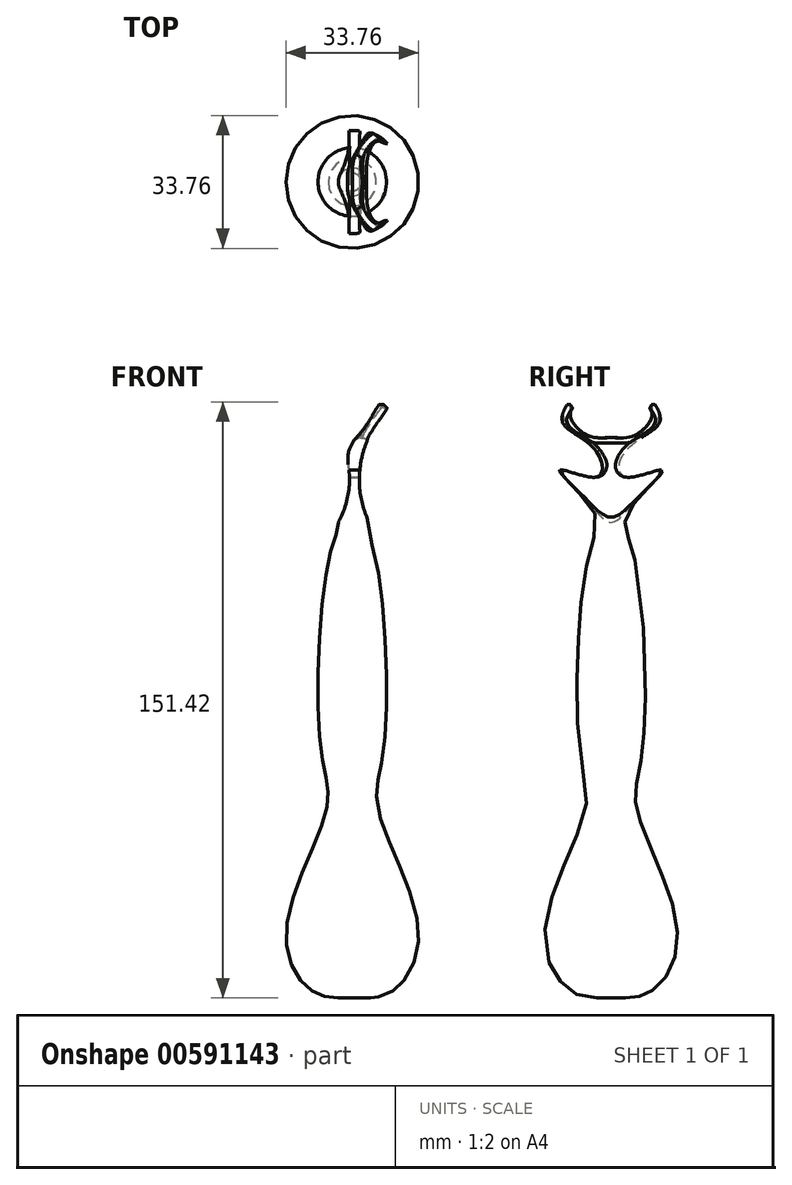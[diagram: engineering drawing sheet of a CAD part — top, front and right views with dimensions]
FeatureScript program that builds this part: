
annotation { "Feature Type Name" : "Feature", "Feature Type Description" : "" }
export const myFeature = defineFeature(function(context is Context, id is Id, definition is map)
    precondition{}
    {
        {
            var Q0;
            Q0=qCreatedBy(makeId("Front.planeOp"),FACE);
            var sketch = newSketch(context, id + "F0", { "sketchPlane" : qUnion([Q0])});
            skLineSegment(sketch, "E0", {"start": v(0, -65.62) * mm, "end": v(0, 64.38) * mm});
            skFitSpline(sketch, "E1", {"points": [v(0, 64.38) * mm, v(-6.2, 64.38) * mm, v(-11.91, 69.45) * mm, v(-12.75, 72.42) * mm], "startDerivative": vector(-17.4, -3.4) * mm, "endDerivative": vector(-1.12, 11.07) * mm});
            skLineSegment(sketch, "E2", {"start": v(-12.75, 72.42) * mm, "end": v(-13.04, 72.42) * mm});
            skFitSpline(sketch, "E3", {"points": [v(-13.04, 72.42) * mm, v(-12.75, 67.5) * mm, v(-4.14, 60.95) * mm, v(-3.52, 54.06) * mm, v(-13.04, 55.7) * mm, v(-4.48, 45.36) * mm, v(-5.61, 34.57) * mm, v(-7.9, -15.91) * mm, v(-6.5, -30.44) * mm, v(-16.85, -61.67) * mm, v(-9.69, -77) * mm, v(0, -78.19) * mm], "startDerivative": vector(-21.06, -99.85) * mm, "endDerivative": vector(134.3, 10.78) * mm});
            skLineSegment(sketch, "E4", {"start": v(0, -78.19) * mm, "end": v(0, -65.62) * mm});
            skSolve(sketch);
        }
        {
            var Q0;
            Q0=makeQuery(id+"F0.imprint","IMPRINT",FACE,{"disambiguationData":[TD([[makeQuery(id+"F0.imprint","IMPRINT",EDGE,{"derivedFrom":sQuery(id+"F0.wireOp",EDGE,"E0")}),1.0]])]});
            var Q1;
            Q1=sQuery(id+"F0.wireOp",EDGE,"E0");
            revolve(context, id + "F1", {"entities" : qUnion([Q0]), "axis" : qUnion([Q1]), "revolveType" : RevolveType.FULL});
        }
        {
            var Q0;
            Q0=qCreatedBy(makeId("Front.planeOp"),FACE);
            var sketch = newSketch(context, id + "F2", { "sketchPlane" : qUnion([Q0])});
            skCircle(sketch, "E5", {"center": v(-23.06, 53.34) * mm, "radius": 22.34 * mm});
            skCircle(sketch, "E6", {"center": v(26.82, 53.34) * mm, "radius": 25.03 * mm});
            skSolve(sketch);
        }
        {
            var Q0;
            Q0 = qSketchRegion(id + "F2", true);
            var Q1;
            Q1=makeQuery(id+"F2.imprint","IMPRINT",FACE,{"disambiguationData":[TD([[makeQuery(id+"F2.imprint","IMPRINT",EDGE,{"derivedFrom":sQuery(id+"F2.wireOp",EDGE,"E6")}),1.0]])]});
            extrude(context, id + "F3", {"entities" : qUnion([Q0, Q1]), "operationType" : NewBodyOperationType.REMOVE, "endBound" : BoundingType.SYMMETRIC, "oppositeDirection" : true, "depth" : 59.2 * mm, "offsetDistance" : 25 * mm});
        }
        {
            var Q0;
            Q0=qCreatedBy(makeId("Front.planeOp"),FACE);
            var sketch = newSketch(context, id + "F4", { "sketchPlane" : qUnion([Q0])});
            skCircle(sketch, "E7", {"center": v(-19.45, 83.07) * mm, "radius": 28.02 * mm});
            skSolve(sketch);
        }
        {
            var Q0;
            Q0=makeQuery(id+"F4.imprint","IMPRINT",FACE,{"disambiguationData":[TD([[makeQuery(id+"F4.imprint","IMPRINT",EDGE,{"derivedFrom":sQuery(id+"F4.wireOp",EDGE,"E7")}),1.0]])]});
            extrude(context, id + "F5", {"entities" : qUnion([Q0]), "operationType" : NewBodyOperationType.REMOVE, "endBound" : BoundingType.SYMMETRIC, "depth" : 90.8 * mm, "offsetDistance" : 25 * mm});
        }
        {
            var Q0;
            Q0=makeQuery(id+"F5.boolean.opBoolean","INTERSECT",EDGE,{"derivedFrom":[makeQuery(id+"F3.boolean.opBoolean","COPY",FACE,{"derivedFrom":makeQuery(id+"F3.opExtrude","SWEPT_FACE",FACE,{"disambiguationData":[OSD([sQuery(id+"F2.wireOp",EDGE,"E5")])]})}),makeQuery(id+"F5.opExtrude","SWEPT_FACE",FACE,{"disambiguationData":[OSD([sQuery(id+"F4.wireOp",EDGE,"E7")])]})]});
            fillet(context, id + "F6", {"entities" : qUnion([Q0]), "radius" : 8.05 * mm, "tangentPropagation" : true, "allowEdgeOverflow" : false});
        }
        {
            var Q0;
            Q0=qCreatedBy(makeId("Right.planeOp"),FACE);
            var sketch = newSketch(context, id + "F7", { "sketchPlane" : qUnion([Q0])});
            skCircle(sketch, "E8", {"center": v(0, 77.34) * mm, "radius": 11.44 * mm});
            skSolve(sketch);
        }
        {
            var Q0;
            Q0 = qSketchRegion(id + "F7", true);
            var Q1;
            Q1=makeQuery(id+"F7.imprint","IMPRINT",FACE,{"disambiguationData":[TD([[makeQuery(id+"F7.imprint","IMPRINT",EDGE,{"derivedFrom":sQuery(id+"F7.wireOp",EDGE,"E8")}),1.0]])]});
            extrude(context, id + "F8", {"entities" : qUnion([Q0, Q1]), "operationType" : NewBodyOperationType.REMOVE, "depth" : 25 * mm, "offsetDistance" : 25 * mm});
        }
        {
            var Q0;
            Q0=makeQuery(id+"F5.boolean.opBoolean","INTERSECT",EDGE,{"derivedFrom":[makeQuery(id+"F1.opRevolve","SWEPT_FACE",FACE,{"disambiguationData":[OSD([sQuery(id+"F0.wireOp",EDGE,"E1")])]}),makeQuery(id+"F5.opExtrude","SWEPT_FACE",FACE,{"disambiguationData":[OSD([sQuery(id+"F4.wireOp",EDGE,"E7")])]})]});
            var Q1;
            Q1=makeQuery(id+"F5.boolean.opBoolean","INTERSECT",EDGE,{"derivedFrom":[makeQuery(id+"F1.opRevolve","SWEPT_FACE",FACE,{"disambiguationData":[OSD([sQuery(id+"F0.wireOp",EDGE,"E1")])]}),makeQuery(id+"F5.opExtrude","SWEPT_FACE",FACE,{"disambiguationData":[OSD([sQuery(id+"F4.wireOp",EDGE,"E7")])]})]});
            var Q2;
            Q2=makeQuery(id+"F6.opFillet","BLEND_EDGE",EDGE,{"disambiguationData":[OD(1.0)],"blendedFrom":[makeQuery(id+"F5.boolean.opBoolean","INTERSECT",EDGE,{"derivedFrom":[makeQuery(id+"F3.boolean.opBoolean","COPY",FACE,{"derivedFrom":makeQuery(id+"F3.opExtrude","SWEPT_FACE",FACE,{"disambiguationData":[OSD([sQuery(id+"F2.wireOp",EDGE,"E5")])]})}),makeQuery(id+"F5.opExtrude","SWEPT_FACE",FACE,{"disambiguationData":[OSD([sQuery(id+"F4.wireOp",EDGE,"E7")])]})]}),makeQuery(id+"F1.opRevolve","SWEPT_FACE",FACE,{"disambiguationData":[OSD([sQuery(id+"F0.wireOp",EDGE,"E1")])]})],"blendedInto":[makeQuery(id+"F1.opRevolve","SWEPT_FACE",FACE,{"disambiguationData":[OSD([sQuery(id+"F0.wireOp",EDGE,"E1")])]})]});
            var Q3;
            Q3=makeQuery(id+"F5.boolean.opBoolean","INTERSECT",EDGE,{"derivedFrom":[makeQuery(id+"F1.opRevolve","SWEPT_FACE",FACE,{"disambiguationData":[OSD([sQuery(id+"F0.wireOp",EDGE,"E1")])]}),makeQuery(id+"F5.opExtrude","SWEPT_FACE",FACE,{"disambiguationData":[OSD([sQuery(id+"F4.wireOp",EDGE,"E7")])]})]});
            var Q4;
            Q4=makeQuery(id+"F6.opFillet","BLEND_EDGE",EDGE,{"disambiguationData":[OD(0.0)],"blendedFrom":[makeQuery(id+"F5.boolean.opBoolean","INTERSECT",EDGE,{"derivedFrom":[makeQuery(id+"F3.boolean.opBoolean","COPY",FACE,{"derivedFrom":makeQuery(id+"F3.opExtrude","SWEPT_FACE",FACE,{"disambiguationData":[OSD([sQuery(id+"F2.wireOp",EDGE,"E5")])]})}),makeQuery(id+"F5.opExtrude","SWEPT_FACE",FACE,{"disambiguationData":[OSD([sQuery(id+"F4.wireOp",EDGE,"E7")])]})]}),makeQuery(id+"F1.opRevolve","SWEPT_FACE",FACE,{"disambiguationData":[OSD([sQuery(id+"F0.wireOp",EDGE,"E1")])]})],"blendedInto":[makeQuery(id+"F1.opRevolve","SWEPT_FACE",FACE,{"disambiguationData":[OSD([sQuery(id+"F0.wireOp",EDGE,"E1")])]})]});
            fillet(context, id + "F9", {"entities" : qUnion([Q0, Q1, Q2, Q3, Q4]), "radius" : 2.63 * mm, "tangentPropagation" : true, "allowEdgeOverflow" : false});
        }
        {
            var Q0;
            Q0=makeQuery(id+"F3.boolean.opBoolean","INTERSECT",EDGE,{"derivedFrom":[makeQuery(id+"F1.opRevolve","SWEPT_FACE",FACE,{"disambiguationData":[OSD([sQuery(id+"F0.wireOp",EDGE,"E1")])]}),makeQuery(id+"F3.opExtrude","SWEPT_FACE",FACE,{"disambiguationData":[OSD([sQuery(id+"F2.wireOp",EDGE,"E6")])]})]});
            fillet(context, id + "F10", {"entities" : qUnion([Q0]), "radius" : 1 * mm, "tangentPropagation" : true, "allowEdgeOverflow" : false});
        }
    });
